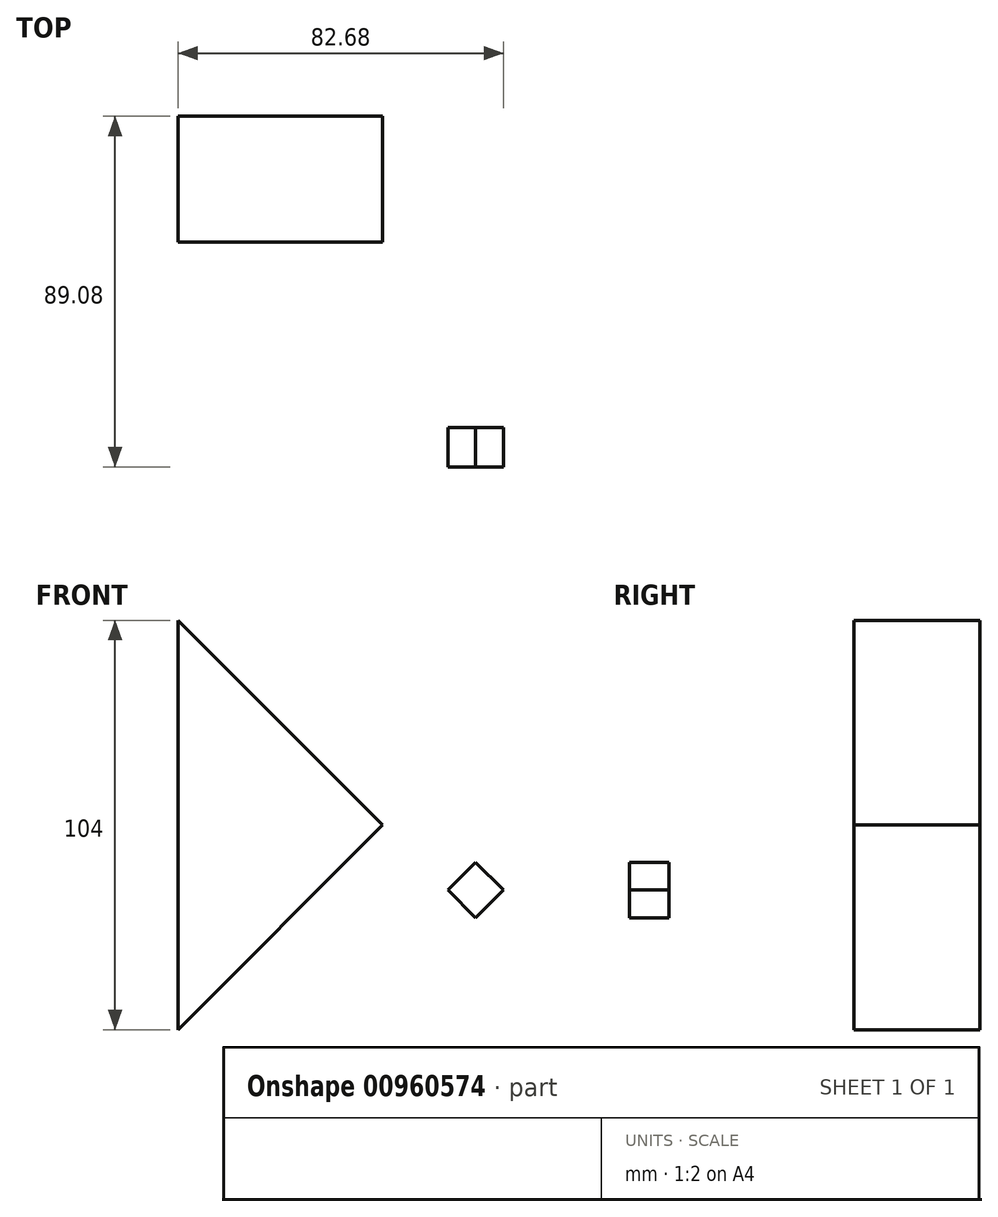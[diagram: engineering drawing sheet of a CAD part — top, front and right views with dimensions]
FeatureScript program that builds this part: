
annotation { "Feature Type Name" : "Feature", "Feature Type Description" : "" }
export const myFeature = defineFeature(function(context is Context, id is Id, definition is map)
    precondition{}
    {
        {
            var Q0;
            Q0=qCreatedBy(makeId("Top.planeOp"),FACE);
            var sketch = newSketch(context, id + "F0", { "sketchPlane" : qUnion([Q0])});
            skLineSegment(sketch, "E0.bottom", {"start": v(26, -16) * mm, "end": v(-26, -16) * mm});
            skLineSegment(sketch, "E0.top", {"start": v(26, 16) * mm, "end": v(-26, 16) * mm});
            skLineSegment(sketch, "E0.left", {"start": v(26, -16) * mm, "end": v(26, 16) * mm});
            skLineSegment(sketch, "E0.right", {"start": v(-26, -16) * mm, "end": v(-26, 16) * mm});
            skPoint(sketch, "E0.middle", {"position": v(0, 0) * mm});
            skSolve(sketch);
        }
        {
            var Q0;
            Q0 = qSketchRegion(id + "F0", true);
            extrude(context, id + "F1", {"entities" : qUnion([Q0]), "depth" : 150 * mm, "offsetDistance" : 25 * mm});
        }
        {
            var Q0;
            Q0=makeQuery(id+"F1.opExtrude","SWEPT_FACE",FACE,{"disambiguationData":[OSD([sQuery(id+"F0.wireOp",EDGE,"E0.bottom")])]});
            var sketch = newSketch(context, id + "F2", { "sketchPlane" : qUnion([Q0])});
            skLineSegment(sketch, "E1", {"start": v(-26, 0) * mm, "end": v(26, 52) * mm});
            skLineSegment(sketch, "E2", {"start": v(26, 52) * mm, "end": v(18.93, 59.07) * mm});
            skLineSegment(sketch, "E3", {"start": v(18.93, 59.07) * mm, "end": v(26, 66.14) * mm});
            skLineSegment(sketch, "E4", {"start": v(26, 66.14) * mm, "end": v(-26, 118.14) * mm});
            skLineSegment(sketch, "E5", {"start": v(-26, 118.14) * mm, "end": v(-26, 0) * mm});
            skLineSegment(sketch, "E6", {"start": v(-26, 0) * mm, "end": v(26, 0) * mm});
            skLineSegment(sketch, "E7", {"start": v(26, 0) * mm, "end": v(26, 52) * mm});
            skLineSegment(sketch, "E8", {"start": v(26, 66.14) * mm, "end": v(26, 150) * mm});
            skLineSegment(sketch, "E9", {"start": v(26, 150) * mm, "end": v(-26, 150) * mm});
            skLineSegment(sketch, "E10", {"start": v(-26, 150) * mm, "end": v(-26, 118.14) * mm});
            skLineSegment(sketch, "E11", {"start": v(26, 66.14) * mm, "end": v(26, 52) * mm});
            skSolve(sketch);
        }
        {
            var Q0;
            Q0=makeQuery(id+"F2.imprint","IMPRINT",FACE,{"disambiguationData":[TD([[makeQuery(id+"F2.imprint","IMPRINT",EDGE,{"derivedFrom":sQuery(id+"F2.wireOp",EDGE,"E1")}),-1.0]])]});
            var Q1;
            Q1=makeQuery(id+"F2.imprint","IMPRINT",FACE,{"disambiguationData":[TD([[makeQuery(id+"F2.imprint","IMPRINT",EDGE,{"derivedFrom":sQuery(id+"F2.wireOp",EDGE,"E4")}),-1.0]])]});
            extrude(context, id + "F3", {"entities" : qUnion([Q0, Q1]), "operationType" : NewBodyOperationType.REMOVE, "oppositeDirection" : true, "depth" : 40 * mm, "offsetDistance" : 25 * mm});
        }
        {
            var Q0;
            Q0=makeQuery(id+"F1.opExtrude","SWEPT_FACE",FACE,{"disambiguationData":[OSD([sQuery(id+"F0.wireOp",EDGE,"E0.bottom")])]});
            var sketch = newSketch(context, id + "F4", { "sketchPlane" : qUnion([Q0])});
            skLineSegment(sketch, "E12", {"start": v(26, 66.14) * mm, "end": v(26, 52) * mm});
            skLineSegment(sketch, "E13", {"start": v(26, 52) * mm, "end": v(-26, 0) * mm});
            skLineSegment(sketch, "E14", {"start": v(26, 66.14) * mm, "end": v(-26, 14.14) * mm});
            skLineSegment(sketch, "E15", {"start": v(-26, 14.14) * mm, "end": v(-26, 0) * mm});
            skSolve(sketch);
        }
        {
            var Q0;
            Q0 = qSketchRegion(id + "F4", true);
            extrude(context, id + "F5", {"entities" : qUnion([Q0]), "operationType" : NewBodyOperationType.REMOVE, "oppositeDirection" : true, "depth" : 40 * mm, "offsetDistance" : 25 * mm});
        }
        {
            var Q0;
            Q0=makeQuery(id+"F3.boolean.opBoolean","COPY",FACE,{"derivedFrom":makeQuery(id+"F3.opExtrude","SWEPT_FACE",FACE,{"disambiguationData":[OSD([sQuery(id+"F2.wireOp",EDGE,"E4")])]})});
            var sketch = newSketch(context, id + "F6", { "sketchPlane" : qUnion([Q0])});
            skLineSegment(sketch, "E16", {"start": v(-28.38, -16) * mm, "end": v(-28.38, -16) * mm});
            skLineSegment(sketch, "E17", {"start": v(-28.38, 0) * mm, "end": v(-68.08, 0) * mm});
            skLineSegment(sketch, "E18.bottom", {"start": v(-63.08, 5) * mm, "end": v(-73.08, 5) * mm});
            skLineSegment(sketch, "E18.top", {"start": v(-63.08, -5) * mm, "end": v(-73.08, -5) * mm});
            skLineSegment(sketch, "E18.left", {"start": v(-63.08, 5) * mm, "end": v(-63.08, -5) * mm});
            skLineSegment(sketch, "E18.right", {"start": v(-73.08, 5) * mm, "end": v(-73.08, -5) * mm});
            skPoint(sketch, "E18.middle", {"position": v(-68.08, 0) * mm});
            skSolve(sketch);
        }
        {
            var Q0;
            Q0 = qSketchRegion(id + "F6", true);
            extrude(context, id + "F7", {"entities" : qUnion([Q0]), "operationType" : NewBodyOperationType.ADD, "depth" : 10 * mm, "offsetDistance" : 25 * mm});
        }
    });
